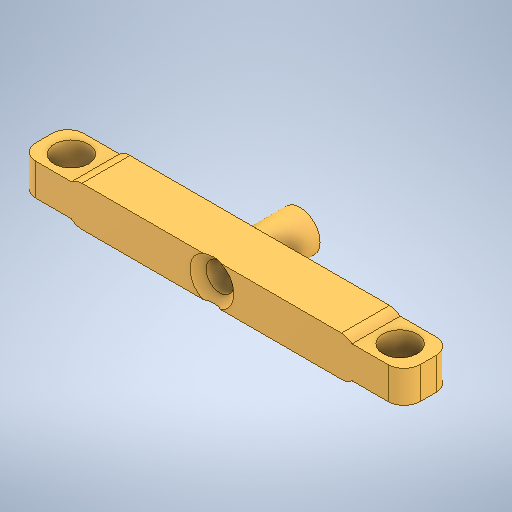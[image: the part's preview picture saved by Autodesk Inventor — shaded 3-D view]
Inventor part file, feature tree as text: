
AUTODESK INVENTOR PART (.ipt)
format: ipt  version: 2025.2 (Build 292293000, 293)  size: 351,232 bytes
history: native  units: in
note: dims shown in document units (in); Inventor stores cm internally (conversion verified against a paired STEP export)
features: fillet x6, move_body x4, extrude x3, sketch x3, direct_edit x1, other x1
ambient origin geometry x8: Origin, YZ Plane, XZ Plane, XY Plane, X Axis, Y Axis, Z Axis, Center Point
bodies: Solid1 (feature_tree)
feature tree (18):
  extrude  "Extrusion1"  Depth=0.1693in
  extrude  "Extrusion2"  Depth=0.2362in
  extrude  "Extrusion3"  Depth=0.2362in
  fillet  "Fillet1"  Radius=0.2362in
  fillet  "Fillet2"  Radius=0.0197in
  direct_edit  "Direct Edit1"
  fillet  "Fillet3"  Radius=0.2362in
  fillet  "Fillet4"  Radius=0.2362in
  fillet  "Fillet5"  Radius=0.2362in
  fillet  "Fillet6"  Radius=0.2362in
  sketch  "Sketch1"  dims[d0=0.1693in d1=0.1693in]
  sketch  "Sketch2"  dims[d2=0.1969in d3=0.0in d4=0.2362in]
  sketch  "Sketch3"  dims[d5=0.2362in d6=0.2362in d7=0.2362in d8=0.0197in d9=0.0in d10=0.2362in d11=0.2362in d12=0.2362in d13=0.2362in d14=0.0197in d15=0.0in d16=0.0787in d17=0.0787in d18=0.0in d19=0.0in d20=0.0197in d21=0.0in d22=0.0in d23=0.0197in d24=0.0787in d25=0.0787in d26=0.0787in d27=0.0787in d28=0.0in d29=0.0in d30=0.0197in d31=0.0in d32=0.0in d33=0.0197in]
  other  "Com_MagnetMount"
  move_body  "Move1"
  move_body  "Move2"
  move_body  "Move3"
  move_body  "Move4"
